# Revit family: Zumtobel CLARIS
name_source: partatom
category: Lighting Fixtures
revit_build: Autodesk Revit 2016 (Build: 20150220_1215(x64)
units: mm (PartAtom-declared; Revit-internal decimal feet)

## family parameters
Cut with Voids When Loaded = No
Host = Face
Light Source = Yes
OmniClass Number = 23.80.70.11
OmniClass Title = Luminaries for Internal Lighting
Part Type = Normal
Room Calculation Point = No
Round Connector Dimension = Use Diameter
Shared = No

## types (4) — shared parameters
Assembly Code = D5020200
Color Filter = 16777215
Description = Pendant LED luminaire
Dimming Lamp Color Temperature Shift = <None>
Emit Shape Visible in Rendering = No
Emit from Rectangle Length = 128 mm
Height = 39 mm
Lamp = LED
Manufacturer = Zumtobel Lighting
Tilt Angle = 90.00°
URL = http://www.zumtobel.com
Voltage = 230 V
Width = 128 mm
zero-valued in all types: Default Elevation

## per-type parameters (varying)
| type | Apparent Load | Emit from Rectangle Width | L 1280 | L 1580 | L 2480 | L 3080 | Length | Model | Photometric Web File |
| CLEVO ID 4400 LED L1280 | 32 VA | 1280 mm | Yes | No | No | No | 1280 mm | 42186125 | D39625_CLEVO_ID_LED_4400-840_L1280_LDO_WH_WHM.IES |
| CLEVO ID 6000 LED L1580 | 43 VA | 1580 mm | No | Yes | No | No | 1580 mm | 42186126 | D39625_CLEVO_ID_LED_6000-840_L1580_LDO_WH_WHM.IES |
| CLEVO ID 12000 LED L3080 | 84 VA | 3080 mm | No | No | No | Yes | 3080 mm | 42186128 | D39625_CLEVO_ID_LED_12000-840_L3080_LDO_WH_WHM.IES |
| CLEVO ID 8800 LED L2480 | 60 VA | 2480 mm | No | No | Yes | No | 2480 mm | 42186127 | D39625_CLEVO_ID_LED_8800-840_L2480_LDO_WH_WHM.IES |

## geometry (parser evidence)
native form markers: Sweep x6
no freeform markers — native parametric forms only
